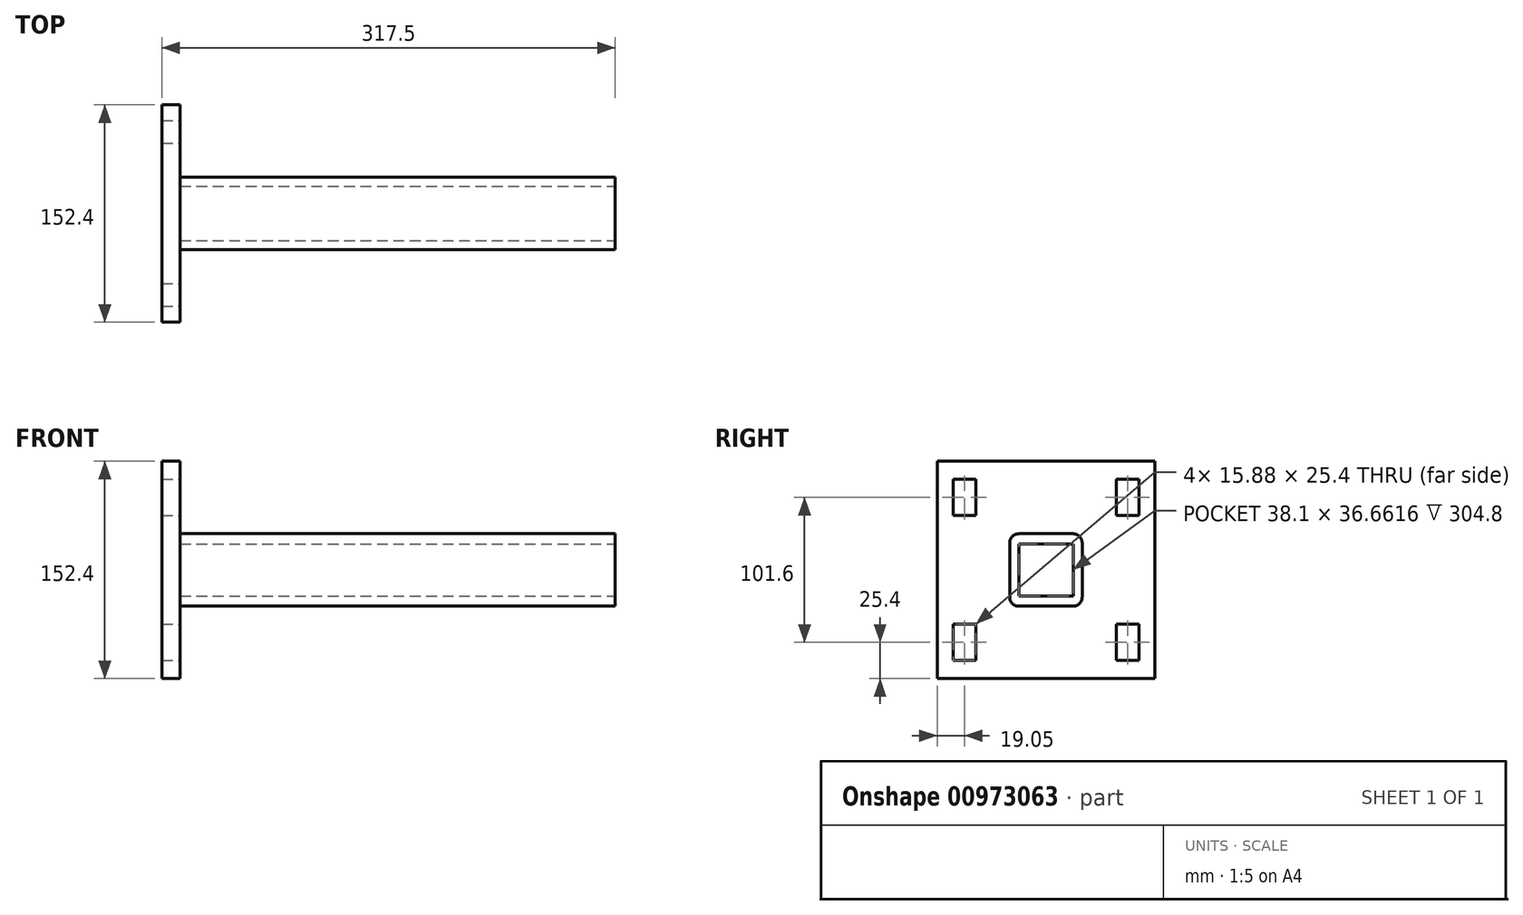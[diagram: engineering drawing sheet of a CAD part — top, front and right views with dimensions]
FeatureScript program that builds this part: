
annotation { "Feature Type Name" : "Feature", "Feature Type Description" : "" }
export const myFeature = defineFeature(function(context is Context, id is Id, definition is map)
    precondition{}
    {
        {
            var Q0;
            Q0=qCreatedBy(makeId("Right.planeOp"),FACE);
            var sketch = newSketch(context, id + "F0", { "sketchPlane" : qUnion([Q0])});
            skLineSegment(sketch, "E0.bottom", {"start": v(76.2, -76.2) * mm, "end": v(-76.2, -76.2) * mm});
            skLineSegment(sketch, "E0.top", {"start": v(76.2, 76.2) * mm, "end": v(-76.2, 76.2) * mm});
            skLineSegment(sketch, "E0.left", {"start": v(76.2, -76.2) * mm, "end": v(76.2, 76.2) * mm});
            skLineSegment(sketch, "E0.right", {"start": v(-76.2, -76.2) * mm, "end": v(-76.2, 76.2) * mm});
            skPoint(sketch, "E0.middle", {"position": v(0, 0) * mm});
            skSolve(sketch);
        }
        {
            var Q0;
            Q0=makeQuery(id+"F0.imprint","IMPRINT",FACE,{"disambiguationData":[TD([[makeQuery(id+"F0.imprint","IMPRINT",EDGE,{"derivedFrom":sQuery(id+"F0.wireOp",EDGE,"E0.bottom")}),-1.0]])]});
            extrude(context, id + "F1", {"entities" : qUnion([Q0]), "oppositeDirection" : true, "depth" : 12.7 * mm, "offsetDistance" : 25.4 * mm});
        }
        {
            var Q0;
            Q0=makeQuery(id+"F1.opExtrude","CAP_FACE",FACE,{"disambiguationData":[OSD([sQuery(id+"F0.wireOp",EDGE,"E0.bottom"),sQuery(id+"F0.wireOp",EDGE,"E0.top"),sQuery(id+"F0.wireOp",EDGE,"E0.left"),sQuery(id+"F0.wireOp",EDGE,"E0.right")])],"isStart":true});
            var sketch = newSketch(context, id + "F2", { "sketchPlane" : qUnion([Q0])});
            skLineSegment(sketch, "E1.bottom", {"start": v(25.4, -25.4) * mm, "end": v(-25.4, -25.4) * mm});
            skLineSegment(sketch, "E1.top", {"start": v(25.4, 25.4) * mm, "end": v(-25.4, 25.4) * mm});
            skLineSegment(sketch, "E1.left", {"start": v(25.4, -25.4) * mm, "end": v(25.4, 25.4) * mm});
            skLineSegment(sketch, "E1.right", {"start": v(-25.4, -25.4) * mm, "end": v(-25.4, 25.4) * mm});
            skPoint(sketch, "E1.middle", {"position": v(0, 0) * mm});
            skSolve(sketch);
        }
        {
            var Q0;
            Q0=makeQuery(id+"F2.imprint","IMPRINT",FACE,{"disambiguationData":[TD([[makeQuery(id+"F2.imprint","IMPRINT",EDGE,{"derivedFrom":sQuery(id+"F2.wireOp",EDGE,"E1.bottom")}),-1.0]])]});
            extrude(context, id + "F3", {"entities" : qUnion([Q0]), "operationType" : NewBodyOperationType.ADD, "depth" : 304.8 * mm, "offsetDistance" : 25.4 * mm});
        }
        {
            var Q0;
            Q0=makeQuery(id+"F3.opExtrude","CAP_FACE",FACE,{"disambiguationData":[OSD([sQuery(id+"F2.wireOp",EDGE,"E1.bottom"),sQuery(id+"F2.wireOp",EDGE,"E1.top"),sQuery(id+"F2.wireOp",EDGE,"E1.left"),sQuery(id+"F2.wireOp",EDGE,"E1.right")])],"isStart":false});
            var sketch = newSketch(context, id + "F4", { "sketchPlane" : qUnion([Q0])});
            skLineSegment(sketch, "E2.bottom", {"start": v(19.05, -18.33) * mm, "end": v(-19.05, -18.33) * mm});
            skLineSegment(sketch, "E2.top", {"start": v(19.05, 18.33) * mm, "end": v(-19.05, 18.33) * mm});
            skLineSegment(sketch, "E2.left", {"start": v(19.05, -18.33) * mm, "end": v(19.05, 18.33) * mm});
            skLineSegment(sketch, "E2.right", {"start": v(-19.05, -18.33) * mm, "end": v(-19.05, 18.33) * mm});
            skPoint(sketch, "E2.middle", {"position": v(0, 0) * mm});
            skSolve(sketch);
        }
        {
            var Q0;
            Q0 = qSketchRegion(id + "F4", true);
            var Q1;
            Q1=makeQuery(id+"F1.opExtrude","CAP_FACE",FACE,{"disambiguationData":[OSD([sQuery(id+"F0.wireOp",EDGE,"E0.bottom"),sQuery(id+"F0.wireOp",EDGE,"E0.top"),sQuery(id+"F0.wireOp",EDGE,"E0.left"),sQuery(id+"F0.wireOp",EDGE,"E0.right")])],"isStart":true});
            extrude(context, id + "F5", {"entities" : qUnion([Q0]), "operationType" : NewBodyOperationType.REMOVE, "endBound" : BoundingType.UP_TO_SURFACE, "oppositeDirection" : true, "depth" : 25.4 * mm, "endBoundEntityFace" : qUnion([Q1]), "offsetDistance" : 25.4 * mm});
        }
        {
            var Q0;
            Q0=makeQuery(id+"F3.opExtrude","SWEPT_EDGE",EDGE,{"disambiguationData":[OSD([sQuery(id+"F2.wireOp",EDGE,"E1.top"),sQuery(id+"F2.wireOp",EDGE,"E1.right")])]});
            var Q1;
            Q1=makeQuery(id+"F3.opExtrude","SWEPT_EDGE",EDGE,{"disambiguationData":[OSD([sQuery(id+"F2.wireOp",EDGE,"E1.top"),sQuery(id+"F2.wireOp",EDGE,"E1.left")])]});
            var Q2;
            Q2=makeQuery(id+"F3.opExtrude","SWEPT_EDGE",EDGE,{"disambiguationData":[OSD([sQuery(id+"F2.wireOp",EDGE,"E1.bottom"),sQuery(id+"F2.wireOp",EDGE,"E1.right")])]});
            var Q3;
            Q3=makeQuery(id+"F3.opExtrude","SWEPT_EDGE",EDGE,{"disambiguationData":[OSD([sQuery(id+"F2.wireOp",EDGE,"E1.bottom"),sQuery(id+"F2.wireOp",EDGE,"E1.left")])]});
            fillet(context, id + "F6", {"entities" : qUnion([Q0, Q1, Q2, Q3]), "radius" : 6.35 * mm, "tangentPropagation" : true, "allowEdgeOverflow" : false});
        }
        {
            var Q0;
            Q0=makeQuery(id+"F1.opExtrude","CAP_FACE",FACE,{"disambiguationData":[OSD([sQuery(id+"F0.wireOp",EDGE,"E0.bottom"),sQuery(id+"F0.wireOp",EDGE,"E0.top"),sQuery(id+"F0.wireOp",EDGE,"E0.left"),sQuery(id+"F0.wireOp",EDGE,"E0.right")])],"isStart":true});
            var sketch = newSketch(context, id + "F7", { "sketchPlane" : qUnion([Q0])});
            skLineSegment(sketch, "E3.bottom", {"start": v(-49.21, 38.1) * mm, "end": v(-65.09, 38.1) * mm});
            skLineSegment(sketch, "E3.top", {"start": v(-49.21, 63.5) * mm, "end": v(-65.09, 63.5) * mm});
            skLineSegment(sketch, "E3.left", {"start": v(-49.21, 38.1) * mm, "end": v(-49.21, 63.5) * mm});
            skLineSegment(sketch, "E3.right", {"start": v(-65.09, 38.1) * mm, "end": v(-65.09, 63.5) * mm});
            skPoint(sketch, "E3.middle", {"position": v(-57.15, 50.8) * mm});
            skLineSegment(sketch, "E4.MirrorCS", {"start": v(49.21, 63.5) * mm, "end": v(65.09, 63.5) * mm});
            skPoint(sketch, "E5.MirrorP", {"position": v(57.15, 50.8) * mm});
            skLineSegment(sketch, "E6.MirrorCS", {"start": v(65.09, 38.1) * mm, "end": v(65.09, 63.5) * mm});
            skLineSegment(sketch, "E7.MirrorCS", {"start": v(49.21, 38.1) * mm, "end": v(65.09, 38.1) * mm});
            skLineSegment(sketch, "E8.MirrorCS", {"start": v(49.21, 38.1) * mm, "end": v(49.21, 63.5) * mm});
            skPoint(sketch, "E9.MirrorP", {"position": v(-57.15, -50.8) * mm});
            skLineSegment(sketch, "E10.MirrorCS", {"start": v(49.21, -63.5) * mm, "end": v(65.09, -63.5) * mm});
            skLineSegment(sketch, "E11.MirrorCS", {"start": v(-65.09, -38.1) * mm, "end": v(-65.09, -63.5) * mm});
            skLineSegment(sketch, "E12.MirrorCS", {"start": v(-49.21, -38.1) * mm, "end": v(-65.09, -38.1) * mm});
            skLineSegment(sketch, "E13.MirrorCS", {"start": v(-49.21, -38.1) * mm, "end": v(-49.21, -63.5) * mm});
            skLineSegment(sketch, "E14.MirrorCS", {"start": v(49.21, -38.1) * mm, "end": v(49.21, -63.5) * mm});
            skLineSegment(sketch, "E15.MirrorCS", {"start": v(65.09, -38.1) * mm, "end": v(65.09, -63.5) * mm});
            skLineSegment(sketch, "E16.MirrorCS", {"start": v(-49.21, -63.5) * mm, "end": v(-65.09, -63.5) * mm});
            skPoint(sketch, "E17.MirrorP", {"position": v(57.15, -50.8) * mm});
            skLineSegment(sketch, "E18.MirrorCS", {"start": v(49.21, -38.1) * mm, "end": v(65.09, -38.1) * mm});
            skSolve(sketch);
        }
        {
            var Q0;
            Q0 = qSketchRegion(id + "F7", true);
            extrude(context, id + "F8", {"entities" : qUnion([Q0]), "operationType" : NewBodyOperationType.REMOVE, "endBound" : BoundingType.THROUGH_ALL, "oppositeDirection" : true, "depth" : 25.4 * mm, "offsetDistance" : 25.4 * mm});
        }
    });
